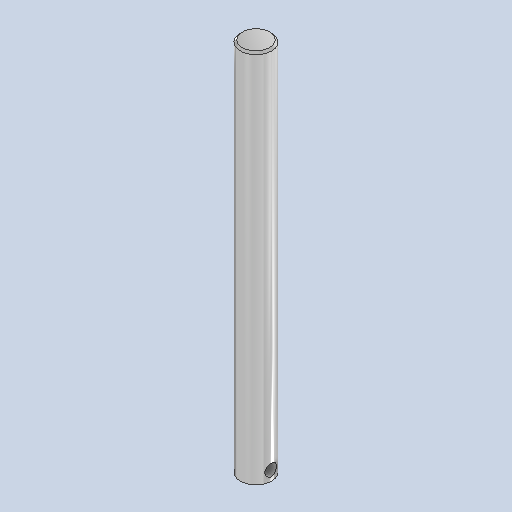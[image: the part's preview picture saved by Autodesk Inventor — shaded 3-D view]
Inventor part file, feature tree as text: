
AUTODESK INVENTOR PART (.ipt)
format: ipt  version: 2025.1 (Build 291241000, 241)  size: 256,000 bytes
history: native  units: mm
features: sketch x2, extrude x1, plane x1, hole x1, chamfer x1
ambient origin geometry x8: Origin, YZ Plane, XZ Plane, XY Plane, X Axis, Y Axis, Z Axis, Center Point
bodies: Solid1 (feature_tree)
feature tree (6):
  extrude  "Extrusion1"  Depth=96.0mm TaperAngle=0.0deg
  plane  "Work Plane1"
  hole  "Hole1"  [1 undecoded]
  chamfer  "Chamfer1"  Distance=0.5mm Angle=45.0deg
  sketch  "Sketch1"  dims[d0=8.0mm d1=96.0mm d2=0.0mm]
  sketch  "Sketch2"  dims[d3=4.0mm d4=2.5mm d5=3.0mm d6=6.0mm d7=4.0mm d8=2.0mm d9=90.0deg d10=8.0mm d11=20.594885mm d12=0.5mm d13=2.0mm d14=45.0deg]
note: 1 required parameter value undecoded (feature->parameter linkage not recoverable at this tier; creation-order binding heuristic only, values carry confidence <= 0.55)
